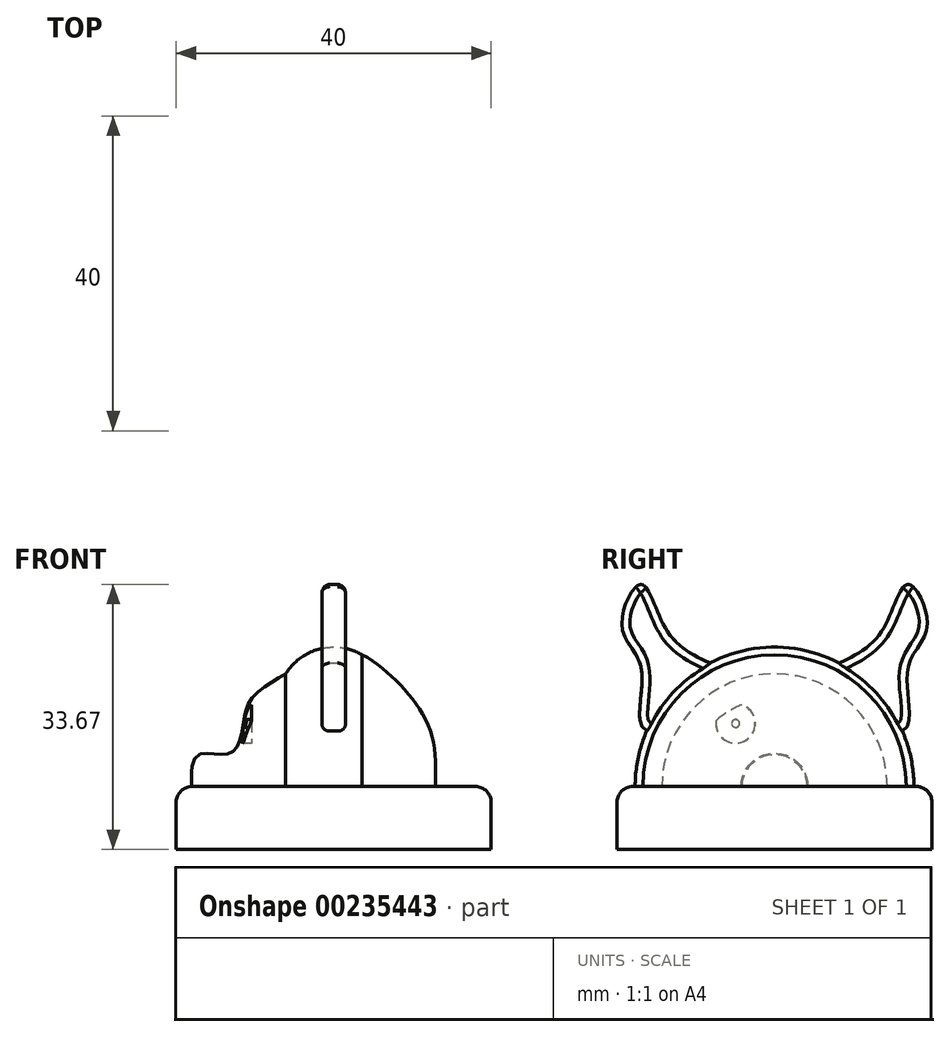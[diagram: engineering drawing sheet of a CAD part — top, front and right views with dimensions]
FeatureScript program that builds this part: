
annotation { "Feature Type Name" : "Feature", "Feature Type Description" : "" }
export const myFeature = defineFeature(function(context is Context, id is Id, definition is map)
    precondition{}
    {
        {
            var Q0;
            Q0=qCreatedBy(makeId("Top.planeOp"),FACE);
            var sketch = newSketch(context, id + "F0", { "sketchPlane" : qUnion([Q0])});
            skLineSegment(sketch, "E0.bottom", {"start": v(20, 20) * mm, "end": v(-20, 20) * mm});
            skLineSegment(sketch, "E0.top", {"start": v(20, -20) * mm, "end": v(-20, -20) * mm});
            skLineSegment(sketch, "E0.left", {"start": v(20, 20) * mm, "end": v(20, -20) * mm});
            skLineSegment(sketch, "E0.right", {"start": v(-20, 20) * mm, "end": v(-20, -20) * mm});
            skPoint(sketch, "E0.middle", {"position": v(0, 0) * mm});
            skSolve(sketch);
        }
        {
            var Q0;
            Q0=makeQuery(id+"F0.imprint","IMPRINT",FACE,{"disambiguationData":[TD([[makeQuery(id+"F0.imprint","IMPRINT",EDGE,{"derivedFrom":sQuery(id+"F0.wireOp",EDGE,"E0.bottom")}),1.0]])]});
            extrude(context, id + "F1", {"entities" : qUnion([Q0]), "depth" : 8 * mm});
        }
        {
            var Q0;
            Q0=makeQuery(id+"F1.opExtrude","CAP_EDGE",EDGE,{"disambiguationData":[OSD([sQuery(id+"F0.wireOp",EDGE,"E0.left")])],"isStart":false});
            var Q1;
            Q1=makeQuery(id+"F1.opExtrude","CAP_EDGE",EDGE,{"disambiguationData":[OSD([sQuery(id+"F0.wireOp",EDGE,"E0.top")])],"isStart":false});
            var Q2;
            Q2=makeQuery(id+"F1.opExtrude","SWEPT_EDGE",EDGE,{"disambiguationData":[OSD([sQuery(id+"F0.wireOp",EDGE,"E0.top"),sQuery(id+"F0.wireOp",EDGE,"E0.left")])]});
            var Q3;
            Q3=makeQuery(id+"F1.opExtrude","CAP_EDGE",EDGE,{"disambiguationData":[OSD([sQuery(id+"F0.wireOp",EDGE,"E0.bottom")])],"isStart":false});
            var Q4;
            Q4=makeQuery(id+"F1.opExtrude","CAP_EDGE",EDGE,{"disambiguationData":[OSD([sQuery(id+"F0.wireOp",EDGE,"E0.right")])],"isStart":false});
            var Q5;
            Q5=makeQuery(id+"F1.opExtrude","SWEPT_EDGE",EDGE,{"disambiguationData":[OSD([sQuery(id+"F0.wireOp",EDGE,"E0.bottom"),sQuery(id+"F0.wireOp",EDGE,"E0.right")])]});
            var Q6;
            Q6=makeQuery(id+"F1.opExtrude","SWEPT_EDGE",EDGE,{"disambiguationData":[OSD([sQuery(id+"F0.wireOp",EDGE,"E0.top"),sQuery(id+"F0.wireOp",EDGE,"E0.right")])]});
            fillet(context, id + "F2", {"entities" : qUnion([Q0, Q1, Q2, Q3, Q4, Q5, Q6]), "radius" : 2 * mm, "tangentPropagation" : true, "allowEdgeOverflow" : false});
        }
        {
            var Q0;
            Q0=qCreatedBy(makeId("Front.planeOp"),FACE);
            var sketch = newSketch(context, id + "F3", { "sketchPlane" : qUnion([Q0])});
            skLineSegment(sketch, "E1.0", {"start": v(-18, 8) * mm, "end": v(18, 8) * mm});
            skLineSegment(sketch, "E2", {"start": v(0, 40.68) * mm, "end": v(0, -9.3) * mm, "construction": true});
            skArc(sketch, "E3", {"start": v(3.6, 24.73) * mm, "mid": v(-1.73, 25.5) * mm, "end": v(-6.09, 22.32) * mm});
            skFitSpline(sketch, "E4", {"points": [v(3.6, 24.73) * mm, v(11.76, 16.36) * mm, v(12.9, 8) * mm], "startDerivative": vector(12.32, -5.35) * mm, "endDerivative": vector(-0.19, -17.45) * mm});
            skFitSpline(sketch, "E5", {"points": [v(-6.09, 22.32) * mm, v(-10.52, 19.01) * mm, v(-11.55, 15.42) * mm, v(-13.19, 12.25) * mm, v(-17.18, 12.04) * mm, v(-18, 8) * mm], "startDerivative": vector(-23.25, -13.25) * mm, "endDerivative": vector(1.03, -26.66) * mm});
            skSolve(sketch);
        }
        {
            var Q0;
            Q0=makeQuery(id+"F3.imprint","IMPRINT",FACE,{"disambiguationData":[TD([[makeQuery(id+"F3.imprint","IMPRINT",EDGE,{"derivedFrom":sQuery(id+"F3.wireOp",EDGE,"E3")}),1.0]])]});
            var Q1;
            Q1=sQuery(id+"F3.wireOp",EDGE,"E1.0");
            revolve(context, id + "F4", {"operationType" : NewBodyOperationType.ADD, "entities" : qUnion([Q0]), "axis" : qUnion([Q1]), "revolveType" : RevolveType.SYMMETRIC, "angle" : 180 * degree});
        }
        {
            var Q0;
            Q0=qCreatedBy(makeId("Right.planeOp"),FACE);
            var sketch = newSketch(context, id + "F5", { "sketchPlane" : qUnion([Q0])});
            skLineSegment(sketch, "E6", {"start": v(0, 52.28) * mm, "end": v(0, 8.7) * mm, "construction": true});
            skFitSpline(sketch, "E7", {"points": [v(-15.97, 14.97) * mm, v(-16.89, 22.77) * mm, v(-19.38, 28.33) * mm, v(-17, 33.67) * mm, v(-13.7, 27.88) * mm, v(-7.82, 23.51) * mm], "startDerivative": vector(-30.75, 5.24) * mm, "endDerivative": vector(30.52, -13.84) * mm});
            skArc(sketch, "E8", {"start": v(-7.82, 23.51) * mm, "mid": v(-12.64, 19.95) * mm, "end": v(-15.97, 14.97) * mm});
            skArc(sketch, "E9.MirrorCS", {"start": v(7.82, 23.51) * mm, "mid": v(12.64, 19.95) * mm, "end": v(15.97, 14.97) * mm});
            skFitSpline(sketch, "E10.MirrorCS", {"points": [v(15.97, 14.97) * mm, v(16.89, 22.77) * mm, v(19.38, 28.33) * mm, v(17, 33.67) * mm, v(13.7, 27.88) * mm, v(7.82, 23.51) * mm], "startDerivative": vector(30.75, 5.24) * mm, "endDerivative": vector(-30.52, -13.84) * mm});
            skSolve(sketch);
        }
        {
            var Q0;
            Q0=makeQuery(id+"F1.opExtrude","SWEPT_FACE",FACE,{"disambiguationData":[OSD([sQuery(id+"F0.wireOp",EDGE,"E0.right")])]});
            var sketch = newSketch(context, id + "F6", { "sketchPlane" : qUnion([Q0])});
            skArc(sketch, "E11.0", {"start": v(14.32, 8) * mm, "mid": v(0, 22.32) * mm, "end": v(-14.32, 8) * mm});
            skCircle(sketch, "E12", {"center": v(4.94, 16) * mm, "radius": 2.5 * mm});
            skCircle(sketch, "E13.MirrorC", {"center": v(-4.94, 16) * mm, "radius": 2.5 * mm});
            skCircle(sketch, "E14", {"center": v(4.94, 16) * mm, "radius": 0.5 * mm});
            skCircle(sketch, "E15.MirrorC", {"center": v(-4.94, 16) * mm, "radius": 0.5 * mm});
            skSolve(sketch);
        }
        {
            var Q0;
            Q0=makeQuery(id+"F6.imprint","IMPRINT",FACE,{"disambiguationData":[TD([[makeQuery(id+"F6.imprint","IMPRINT",EDGE,{"derivedFrom":sQuery(id+"F6.wireOp",EDGE,"E13.MirrorC")}),-1.0]])]});
            var Q1;
            Q1=makeQuery(id+"F6.imprint","IMPRINT",FACE,{"disambiguationData":[TD([[makeQuery(id+"F6.imprint","IMPRINT",EDGE,{"derivedFrom":sQuery(id+"F6.wireOp",EDGE,"E12")}),1.0]])]});
            extrude(context, id + "F7", {"entities" : qUnion([Q0, Q1]), "operationType" : NewBodyOperationType.REMOVE, "oppositeDirection" : true, "depth" : 9.6 * mm});
        }
        {
            var Q0;
            Q0=makeQuery(id+"F5.imprint","IMPRINT",FACE,{"disambiguationData":[TD([[makeQuery(id+"F5.imprint","IMPRINT",EDGE,{"derivedFrom":sQuery(id+"F5.wireOp",EDGE,"E10.MirrorCS")}),1.0]])]});
            var Q1;
            Q1=makeQuery(id+"F5.imprint","IMPRINT",FACE,{"disambiguationData":[TD([[makeQuery(id+"F5.imprint","IMPRINT",EDGE,{"derivedFrom":sQuery(id+"F5.wireOp",EDGE,"E7")}),-1.0]])]});
            extrude(context, id + "F8", {"entities" : qUnion([Q0, Q1]), "operationType" : NewBodyOperationType.ADD, "endBound" : BoundingType.SYMMETRIC, "depth" : 3 * mm});
        }
        {
            var Q0;
            Q0=makeQuery(id+"F8.opExtrude","CAP_EDGE",EDGE,{"disambiguationData":[OSD([sQuery(id+"F5.wireOp",EDGE,"E7")])],"isStart":true});
            var Q1;
            Q1=makeQuery(id+"F8.opExtrude","CAP_EDGE",EDGE,{"disambiguationData":[OSD([sQuery(id+"F5.wireOp",EDGE,"E7")])],"isStart":false});
            var Q2;
            Q2=makeQuery(id+"F8.opExtrude","CAP_EDGE",EDGE,{"disambiguationData":[OSD([sQuery(id+"F5.wireOp",EDGE,"E10.MirrorCS")])],"isStart":true});
            var Q3;
            Q3=makeQuery(id+"F8.opExtrude","CAP_EDGE",EDGE,{"disambiguationData":[OSD([sQuery(id+"F5.wireOp",EDGE,"E10.MirrorCS")])],"isStart":false});
            fillet(context, id + "F9", {"entities" : qUnion([Q0, Q1, Q2, Q3]), "radius" : 1 * mm, "tangentPropagation" : true, "allowEdgeOverflow" : false});
        }
    });
